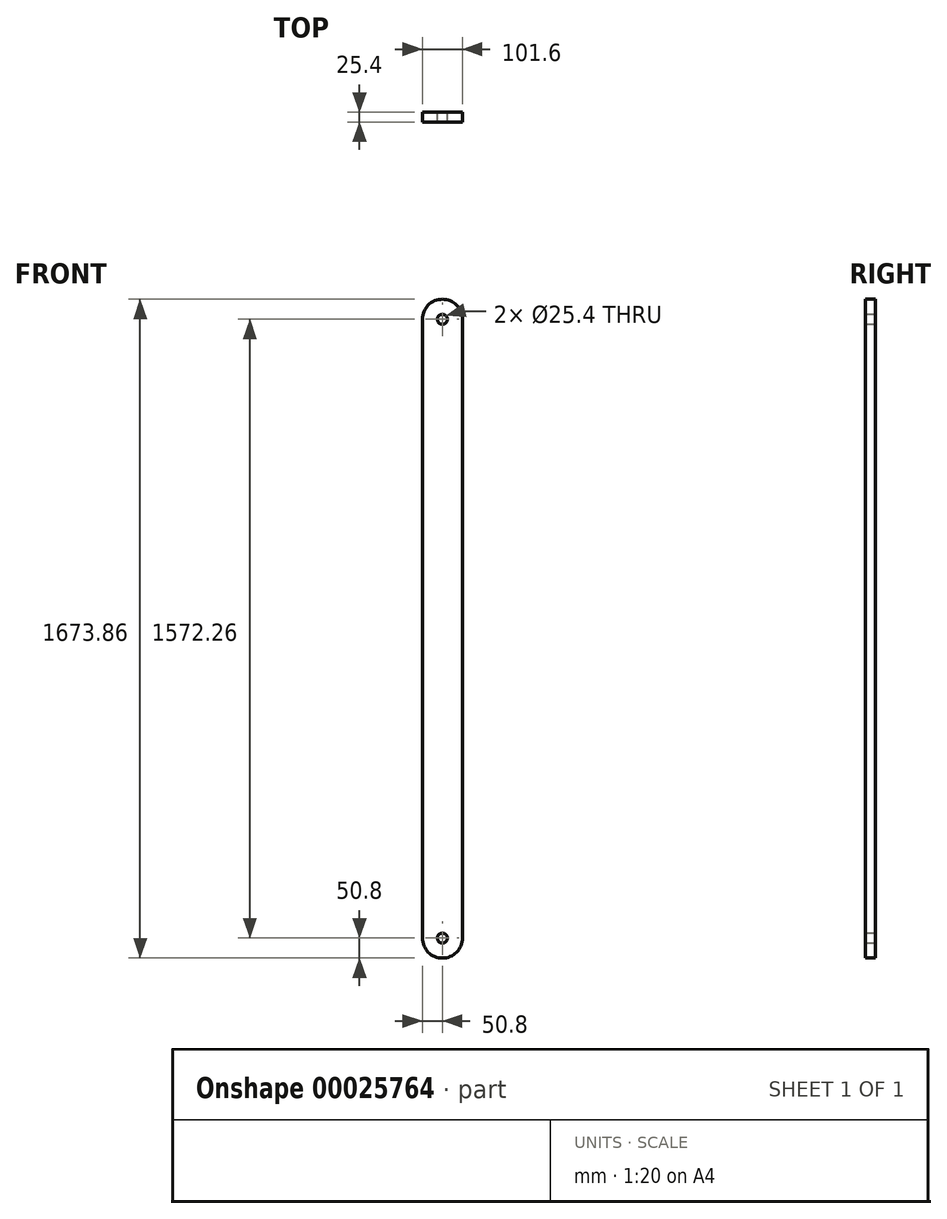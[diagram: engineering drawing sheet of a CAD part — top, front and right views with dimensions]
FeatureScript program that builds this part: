
annotation { "Feature Type Name" : "Feature", "Feature Type Description" : "" }
export const myFeature = defineFeature(function(context is Context, id is Id, definition is map)
    precondition{}
    {
        {
            var Q0;
            Q0=qCreatedBy(makeId("Front.planeOp"),FACE);
            var sketch = newSketch(context, id + "F0", { "sketchPlane" : qUnion([Q0])});
            skCircle(sketch, "E0", {"center": v(0, 0) * mm, "radius": 12.7 * mm});
            skLineSegment(sketch, "E1", {"start": v(50.8, 0) * mm, "end": v(50.8, 1572.26) * mm});
            skLineSegment(sketch, "E2", {"start": v(-50.8, 0) * mm, "end": v(-50.8, 1572.26) * mm});
            skArc(sketch, "E3", {"start": v(-50.8, 0) * mm, "mid": v(0, -50.8) * mm, "end": v(50.8, 0) * mm});
            skArc(sketch, "E4", {"start": v(50.8, 1572.26) * mm, "mid": v(0, 1623.06) * mm, "end": v(-50.8, 1572.26) * mm});
            skCircle(sketch, "E5", {"center": v(0, 1572.26) * mm, "radius": 12.7 * mm});
            skSolve(sketch);
        }
        {
            var Q0;
            Q0=qSketchRegion(id+"F0",true);
            extrude(context, id + "F1", {"entities" : qUnion([Q0]), "depth" : 25.4 * mm});
        }
    });
